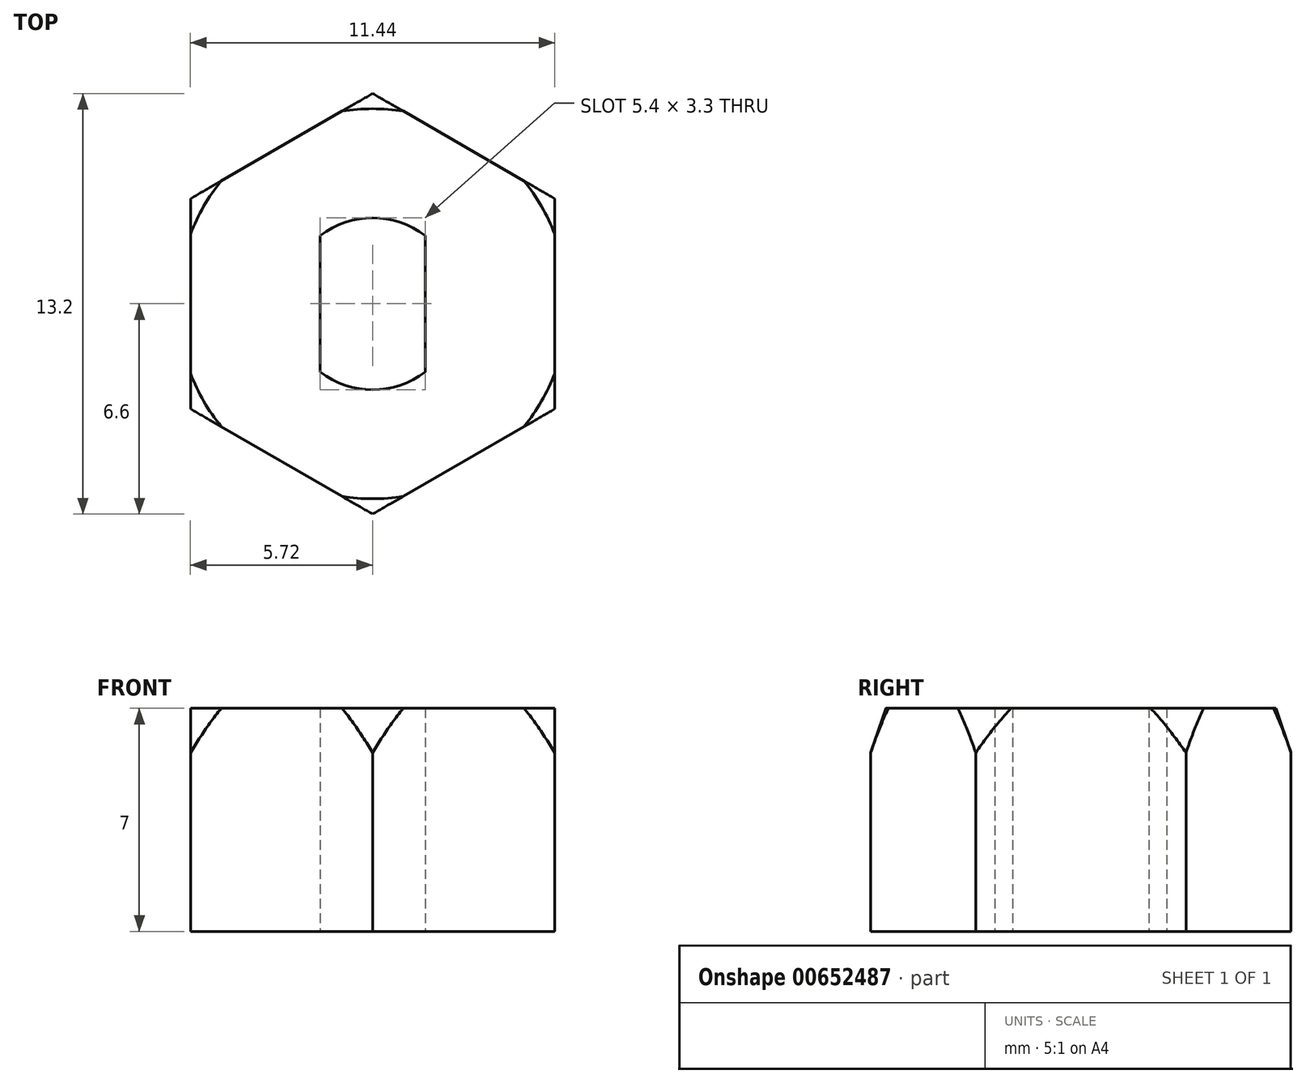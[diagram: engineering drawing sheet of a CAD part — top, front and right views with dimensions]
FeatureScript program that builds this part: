
annotation { "Feature Type Name" : "Feature", "Feature Type Description" : "" }
export const myFeature = defineFeature(function(context is Context, id is Id, definition is map)
    precondition{}
    {
        {
            var Q0;
            Q0=qCreatedBy(makeId("Top.planeOp"),FACE);
            var sketch = newSketch(context, id + "F0", { "sketchPlane" : qUnion([Q0])});
            skCircle(sketch, "E0", {"center": v(0, 0) * mm, "radius": 2.7 * mm});
            skLineSegment(sketch, "E1", {"start": v(-1.65, -2.14) * mm, "end": v(-1.65, 2.14) * mm});
            skLineSegment(sketch, "E2", {"start": v(1.65, 2.14) * mm, "end": v(1.65, -2.14) * mm});
            skCircle(sketch, "E3.cCircle", {"center": v(0, 0) * mm, "radius": 6.6 * mm, "construction": true});
            skLineSegment(sketch, "E3.0", {"start": v(0, -6.6) * mm, "end": v(-5.72, -3.3) * mm});
            skLineSegment(sketch, "E3.1", {"start": v(-5.72, -3.3) * mm, "end": v(-5.72, 3.3) * mm});
            skLineSegment(sketch, "E3.2", {"start": v(-5.72, 3.3) * mm, "end": v(0, 6.6) * mm});
            skLineSegment(sketch, "E3.3", {"start": v(0, 6.6) * mm, "end": v(5.72, 3.3) * mm});
            skLineSegment(sketch, "E3.4", {"start": v(5.72, 3.3) * mm, "end": v(5.72, -3.3) * mm});
            skLineSegment(sketch, "E3.5", {"start": v(5.72, -3.3) * mm, "end": v(0, -6.6) * mm});
            skSolve(sketch);
        }
        {
            var Q0;
            Q0=makeQuery(id+"F0.imprint","IMPRINT",FACE,{"disambiguationData":[TD([[makeQuery(id+"F0.imprint","IMPRINT",EDGE,{"derivedFrom":sQuery(id+"F0.wireOp",EDGE,"E3.0")}),-1.0]])]});
            var Q1;
            {var subQ0=sQuery(id+"F0.wireOp",EDGE,"E1");Q1=makeQuery(id+"F0.imprint","IMPRINT",FACE,{"disambiguationData":[TD([[makeQuery(id+"F0.imprint","IMPRINT",EDGE,{"derivedFrom":subQ0}),1.0]])]});}
            var Q2;
            {var subQ0=sQuery(id+"F0.wireOp",EDGE,"E2");Q2=makeQuery(id+"F0.imprint","IMPRINT",FACE,{"disambiguationData":[TD([[makeQuery(id+"F0.imprint","IMPRINT",EDGE,{"derivedFrom":subQ0}),1.0]])]});}
            extrude(context, id + "F1", {"entities" : qUnion([Q0, Q1, Q2]), "depth" : 7 * mm, "offsetDistance" : 25 * mm});
        }
        {
            var Q0;
            Q0=qCreatedBy(makeId("Right.planeOp"),FACE);
            var sketch = newSketch(context, id + "F2", { "sketchPlane" : qUnion([Q0])});
            skLineSegment(sketch, "E4", {"start": v(-5.57, 8.62) * mm, "end": v(-7.08, 4.2) * mm});
            skLineSegment(sketch, "E5", {"start": v(-7.08, 4.2) * mm, "end": v(-7.08, 8.62) * mm});
            skLineSegment(sketch, "E6", {"start": v(-7.08, 8.62) * mm, "end": v(-5.57, 8.62) * mm});
            skLineSegment(sketch, "E7", {"start": v(0, 0) * mm, "end": v(0, 9.84) * mm});
            skSolve(sketch);
        }
        {
            var Q0;
            Q0=qSketchRegion(id+"F2",true);
            var Q1;
            Q1=sQuery(id+"F2.wireOp",EDGE,"E7");
            revolve(context, id + "F3", {"operationType" : NewBodyOperationType.REMOVE, "entities" : qUnion([Q0]), "axis" : qUnion([Q1]), "revolveType" : RevolveType.FULL, "oppositeDirection" : true});
        }
    });
